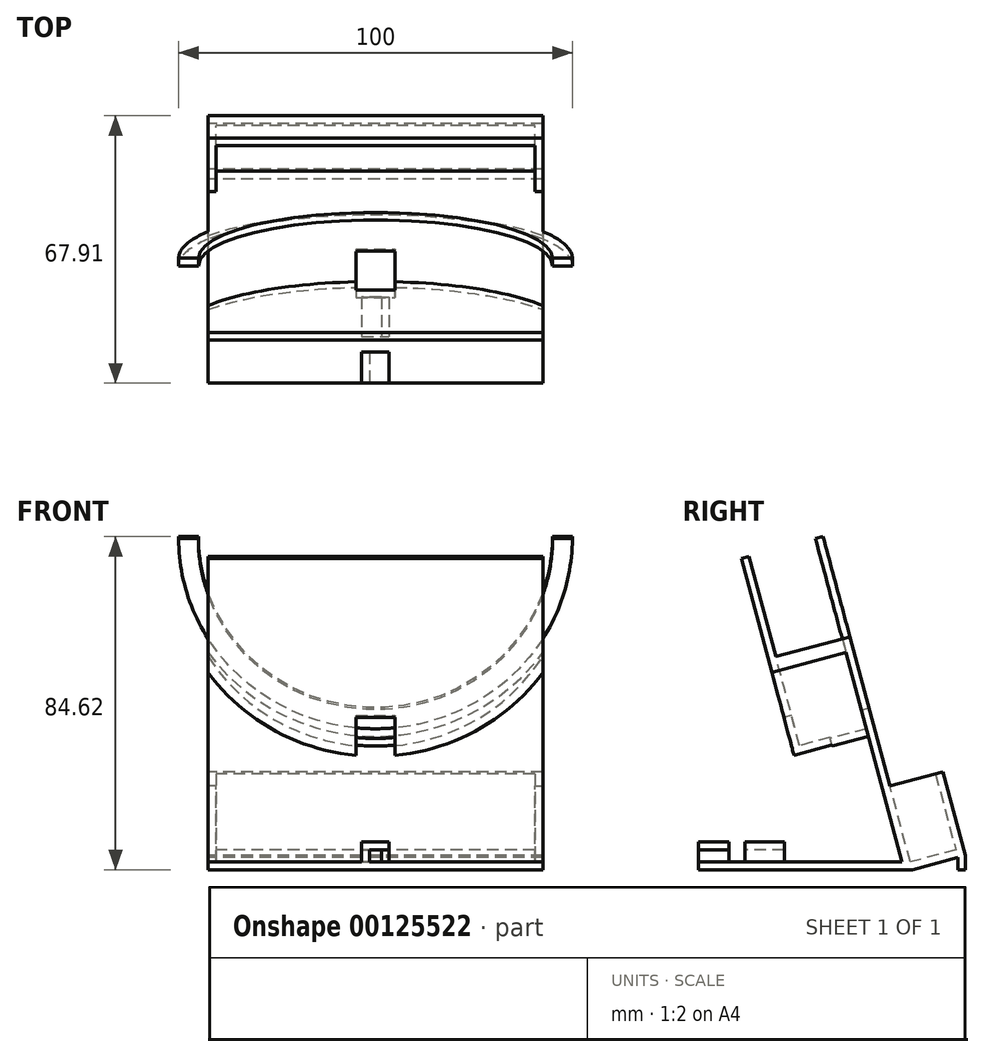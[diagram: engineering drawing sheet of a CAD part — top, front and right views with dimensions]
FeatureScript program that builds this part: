
annotation { "Feature Type Name" : "Feature", "Feature Type Description" : "" }
export const myFeature = defineFeature(function(context is Context, id is Id, definition is map)
    precondition{}
    {
        {
            var Q0;
            Q0=qCreatedBy(makeId("Right.planeOp"),FACE);
            var sketch = newSketch(context, id + "F0", { "sketchPlane" : qUnion([Q0])});
            skLineSegment(sketch, "E0", {"start": v(-54.39, 0) * mm, "end": v(0, 0) * mm});
            skLineSegment(sketch, "E1", {"start": v(-0.52, 1.93) * mm, "end": v(-23.24, 86.73) * mm});
            skLineSegment(sketch, "E2", {"start": v(-23.24, 86.73) * mm, "end": v(-25.17, 86.21) * mm});
            skLineSegment(sketch, "E3", {"start": v(-25.17, 86.21) * mm, "end": v(-2.6, 2) * mm});
            skLineSegment(sketch, "E4", {"start": v(-54.39, 0) * mm, "end": v(-54.39, 2) * mm});
            skLineSegment(sketch, "E5", {"start": v(-54.39, 2) * mm, "end": v(-2.6, 2) * mm});
            skLineSegment(sketch, "E6", {"start": v(0, 0) * mm, "end": v(11.52, 3.09) * mm});
            skLineSegment(sketch, "E7", {"start": v(13.52, 3.62) * mm, "end": v(13, 5.56) * mm});
            skLineSegment(sketch, "E8", {"start": v(11.07, 5.04) * mm, "end": v(-0.52, 1.93) * mm});
            skLineSegment(sketch, "E9", {"start": v(13, 5.56) * mm, "end": v(7.83, 24.87) * mm});
            skLineSegment(sketch, "E10", {"start": v(7.83, 24.87) * mm, "end": v(5.9, 24.36) * mm});
            skLineSegment(sketch, "E11", {"start": v(5.9, 24.36) * mm, "end": v(11.07, 5.04) * mm});
            skLineSegment(sketch, "E12", {"start": v(-65.45, 0) * mm, "end": v(42.7, 0) * mm, "construction": true});
            skLineSegment(sketch, "E13", {"start": v(13.52, 3.62) * mm, "end": v(13.52, 0) * mm});
            skLineSegment(sketch, "E14", {"start": v(13.52, 0) * mm, "end": v(11.52, 0) * mm});
            skLineSegment(sketch, "E15", {"start": v(11.52, 0) * mm, "end": v(11.52, 3.09) * mm});
            skSolve(sketch);
        }
        {
            var Q0;
            Q0 = qSketchRegion(id + "F0", true);
            extrude(context, id + "F1", {"entities" : qUnion([Q0]), "depth" : 85 * mm});
        }
        {
            var Q0;
            Q0=makeQuery(id+"F1.opExtrude","CAP_FACE",FACE,{"disambiguationData":[OSD([sQuery(id+"F0.wireOp",EDGE,"E0"),sQuery(id+"F0.wireOp",EDGE,"E1"),sQuery(id+"F0.wireOp",EDGE,"E2"),sQuery(id+"F0.wireOp",EDGE,"E3"),sQuery(id+"F0.wireOp",EDGE,"E4"),sQuery(id+"F0.wireOp",EDGE,"E5"),sQuery(id+"F0.wireOp",EDGE,"E6"),sQuery(id+"F0.wireOp",EDGE,"E7"),sQuery(id+"F0.wireOp",EDGE,"E8"),sQuery(id+"F0.wireOp",EDGE,"E9"),sQuery(id+"F0.wireOp",EDGE,"E10"),sQuery(id+"F0.wireOp",EDGE,"E11"),sQuery(id+"F0.wireOp",EDGE,"E13"),sQuery(id+"F0.wireOp",EDGE,"E14"),sQuery(id+"F0.wireOp",EDGE,"E15")])],"isStart":false});
            var sketch = newSketch(context, id + "F2", { "sketchPlane" : qUnion([Q0])});
            skLineSegment(sketch, "E16.0", {"start": v(5.9, 24.36) * mm, "end": v(11.07, 5.04) * mm});
            skLineSegment(sketch, "E16.1", {"start": v(11.07, 5.04) * mm, "end": v(-0.52, 1.93) * mm});
            skLineSegment(sketch, "E16.2", {"start": v(-0.52, 1.93) * mm, "end": v(-23.24, 86.73) * mm});
            skPoint(sketch, "E16.3", {"position": v(5.9, 24.36) * mm});
            skLineSegment(sketch, "E17", {"start": v(5.9, 24.36) * mm, "end": v(-5.7, 21.25) * mm});
            skSolve(sketch);
        }
        {
            var Q0;
            Q0 = qSketchRegion(id + "F2", true);
            extrude(context, id + "F3", {"entities" : qUnion([Q0]), "operationType" : NewBodyOperationType.ADD, "oppositeDirection" : true, "depth" : 2 * mm});
        }
        {
            var Q0;
            Q0=makeQuery(id+"F1.opExtrude","CAP_FACE",FACE,{"disambiguationData":[OSD([sQuery(id+"F0.wireOp",EDGE,"E0"),sQuery(id+"F0.wireOp",EDGE,"E1"),sQuery(id+"F0.wireOp",EDGE,"E2"),sQuery(id+"F0.wireOp",EDGE,"E3"),sQuery(id+"F0.wireOp",EDGE,"E4"),sQuery(id+"F0.wireOp",EDGE,"E5"),sQuery(id+"F0.wireOp",EDGE,"E6"),sQuery(id+"F0.wireOp",EDGE,"E7"),sQuery(id+"F0.wireOp",EDGE,"E8"),sQuery(id+"F0.wireOp",EDGE,"E9"),sQuery(id+"F0.wireOp",EDGE,"E10"),sQuery(id+"F0.wireOp",EDGE,"E11"),sQuery(id+"F0.wireOp",EDGE,"E13"),sQuery(id+"F0.wireOp",EDGE,"E14"),sQuery(id+"F0.wireOp",EDGE,"E15")])],"isStart":true});
            var sketch = newSketch(context, id + "F4", { "sketchPlane" : qUnion([Q0])});
            skLineSegment(sketch, "E18.0", {"start": v(-5.9, 24.36) * mm, "end": v(-11.07, 5.04) * mm});
            skLineSegment(sketch, "E18.1", {"start": v(-11.07, 5.04) * mm, "end": v(0.52, 1.93) * mm});
            skLineSegment(sketch, "E18.2", {"start": v(0.52, 1.93) * mm, "end": v(23.24, 86.73) * mm});
            skLineSegment(sketch, "E19", {"start": v(-5.9, 24.36) * mm, "end": v(5.7, 21.25) * mm});
            skSolve(sketch);
        }
        {
            var Q0;
            Q0 = qSketchRegion(id + "F4", true);
            extrude(context, id + "F5", {"entities" : qUnion([Q0]), "operationType" : NewBodyOperationType.ADD, "oppositeDirection" : true, "depth" : 2 * mm});
        }
        {
            var Q0;
            Q0=makeQuery(id+"F1.opExtrude","SWEPT_FACE",FACE,{"disambiguationData":[OSD([sQuery(id+"F0.wireOp",EDGE,"E3")])]});
            var sketch = newSketch(context, id + "F6", { "sketchPlane" : qUnion([Q0])});
            skLineSegment(sketch, "E20.0", {"start": v(85, 89.79) * mm, "end": v(0, 89.79) * mm});
            skLineSegment(sketch, "E21.0", {"start": v(0, 89.79) * mm, "end": v(0, 2.6) * mm});
            skLineSegment(sketch, "E22", {"start": v(0, 98.6) * mm, "end": v(85, 98.6) * mm, "construction": true});
            skLineSegment(sketch, "E23", {"start": v(96.81, 89.79) * mm, "end": v(96.81, 2.6) * mm, "construction": true});
            skPoint(sketch, "E24.endSnap0", {"position": v(42.5, 89.79) * mm});
            skCircle(sketch, "E25", {"center": v(42.5, 87.6) * mm, "radius": 50 * mm});
            skPoint(sketch, "E26", {"position": v(42.5, 37.6) * mm});
            skSolve(sketch);
        }
        {
            var Q0;
            Q0 = qSketchRegion(id + "F6", true);
            extrude(context, id + "F7", {"entities" : qUnion([Q0]), "operationType" : NewBodyOperationType.REMOVE, "oppositeDirection" : true, "depth" : 25 * mm});
        }
        {
            var Q0;
            Q0=makeQuery(id+"F1.opExtrude","SWEPT_FACE",FACE,{"disambiguationData":[OSD([sQuery(id+"F0.wireOp",EDGE,"E3")])]});
            var sketch = newSketch(context, id + "F8", { "sketchPlane" : qUnion([Q0])});
            skArc(sketch, "E27.0", {"start": v(0, 61.27) * mm, "mid": v(42.5, 37.6) * mm, "end": v(85, 61.27) * mm});
            skArc(sketch, "E28.0", {"start": v(0, 57.64) * mm, "mid": v(42.5, 35.6) * mm, "end": v(85, 57.64) * mm});
            skLineSegment(sketch, "E29.0", {"start": v(0, 61.27) * mm, "end": v(0, 2.6) * mm});
            skLineSegment(sketch, "E29.1", {"start": v(85, 61.27) * mm, "end": v(85, 2.6) * mm});
            skSolve(sketch);
        }
        {
            var Q0;
            Q0 = qSketchRegion(id + "F8", true);
            extrude(context, id + "F9", {"entities" : qUnion([Q0]), "operationType" : NewBodyOperationType.ADD, "depth" : 17.5 * mm});
        }
        {
            var Q0;
            Q0=makeQuery(id+"F9.opExtrude","CAP_FACE",FACE,{"disambiguationData":[OSD([sQuery(id+"F8.wireOp",EDGE,"E27.0"),sQuery(id+"F8.wireOp",EDGE,"E28.0"),sQuery(id+"F8.wireOp",EDGE,"E29.0"),sQuery(id+"F8.wireOp",EDGE,"E29.1")])],"isStart":false});
            var sketch = newSketch(context, id + "F10", { "sketchPlane" : qUnion([Q0])});
            skArc(sketch, "E30.0", {"start": v(0, 57.64) * mm, "mid": v(42.5, 35.6) * mm, "end": v(85, 57.64) * mm});
            skLineSegment(sketch, "E30.1", {"start": v(0, 61.27) * mm, "end": v(0, 57.64) * mm});
            skLineSegment(sketch, "E30.2", {"start": v(85, 61.27) * mm, "end": v(85, 57.64) * mm});
            skLineSegment(sketch, "E31", {"start": v(0, 61.27) * mm, "end": v(0, 87.6) * mm});
            skLineSegment(sketch, "E32", {"start": v(85, 61.27) * mm, "end": v(85, 87.6) * mm});
            skLineSegment(sketch, "E33", {"start": v(85, 87.6) * mm, "end": v(0, 87.6) * mm});
            skSolve(sketch);
        }
        {
            var Q0;
            Q0 = qSketchRegion(id + "F10", true);
            extrude(context, id + "F11", {"entities" : qUnion([Q0]), "operationType" : NewBodyOperationType.ADD, "depth" : 2 * mm});
        }
        {
            var Q0;
            Q0=makeQuery(id+"F11.opExtrude","CAP_FACE",FACE,{"disambiguationData":[OSD([sQuery(id+"F10.wireOp",EDGE,"E30.0"),sQuery(id+"F10.wireOp",EDGE,"E30.1"),sQuery(id+"F10.wireOp",EDGE,"E30.2"),sQuery(id+"F10.wireOp",EDGE,"E31"),sQuery(id+"F10.wireOp",EDGE,"E32"),sQuery(id+"F10.wireOp",EDGE,"E33")])],"isStart":false});
            var sketch = newSketch(context, id + "F12", { "sketchPlane" : qUnion([Q0])});
            skArc(sketch, "E34.0", {"start": v(0, 57.64) * mm, "mid": v(42.5, 35.6) * mm, "end": v(85, 57.64) * mm});
            skLineSegment(sketch, "E35", {"start": v(0, 57.64) * mm, "end": v(85, 57.64) * mm, "construction": true});
            skPoint(sketch, "E36", {"position": v(42.5, 57.64) * mm});
            skLineSegment(sketch, "E37", {"start": v(42.5, 57.64) * mm, "end": v(42.5, 35.6) * mm, "construction": true});
            skLineSegment(sketch, "E38", {"start": v(47.5, 57.64) * mm, "end": v(47.5, 35.85) * mm, "construction": true});
            skLineSegment(sketch, "E39", {"start": v(37.5, 57.64) * mm, "end": v(37.5, 35.85) * mm, "construction": true});
            skLineSegment(sketch, "E40", {"start": v(37.5, 35.85) * mm, "end": v(37.5, 45.85) * mm});
            skLineSegment(sketch, "E41", {"start": v(37.5, 45.85) * mm, "end": v(47.5, 45.85) * mm});
            skLineSegment(sketch, "E42", {"start": v(47.5, 45.85) * mm, "end": v(47.5, 35.85) * mm});
            skSolve(sketch);
        }
        {
            var Q0;
            Q0 = qSketchRegion(id + "F12", true);
            extrude(context, id + "F13", {"entities" : qUnion([Q0]), "operationType" : NewBodyOperationType.REMOVE, "oppositeDirection" : true, "depth" : 10 * mm});
        }
        {
            var Q0;
            Q0=makeQuery(id+"F1.opExtrude","SWEPT_FACE",FACE,{"disambiguationData":[OSD([sQuery(id+"F0.wireOp",EDGE,"E1")])]});
            var sketch = newSketch(context, id + "F14", { "sketchPlane" : qUnion([Q0])});
            skArc(sketch, "E43.0", {"start": v(7.5, 87.6) * mm, "mid": v(-42.5, 37.6) * mm, "end": v(-92.5, 87.6) * mm});
            skArc(sketch, "E44.0", {"start": v(2.5, 87.6) * mm, "mid": v(-42.5, 42.6) * mm, "end": v(-87.5, 87.6) * mm});
            skPoint(sketch, "E45.orphan", {"position": v(-85, 61.27) * mm});
            skPoint(sketch, "E46.orphan", {"position": v(0, 61.27) * mm});
            skLineSegment(sketch, "E47", {"start": v(-107.52, 87.6) * mm, "end": v(17.74, 87.6) * mm, "construction": true});
            skLineSegment(sketch, "E48", {"start": v(-92.5, 87.6) * mm, "end": v(-87.5, 87.6) * mm});
            skLineSegment(sketch, "E49", {"start": v(2.5, 87.6) * mm, "end": v(7.5, 87.6) * mm});
            skSolve(sketch);
        }
        {
            var Q0;
            Q0 = qSketchRegion(id + "F14", true);
            extrude(context, id + "F15", {"entities" : qUnion([Q0]), "operationType" : NewBodyOperationType.ADD, "oppositeDirection" : true, "depth" : 2 * mm});
        }
        {
            var Q0;
            Q0=makeQuery(id+"F1.opExtrude","SWEPT_FACE",FACE,{"disambiguationData":[OSD([sQuery(id+"F0.wireOp",EDGE,"E5")])]});
            var sketch = newSketch(context, id + "F16", { "sketchPlane" : qUnion([Q0])});
            skLineSegment(sketch, "E50.0", {"start": v(85, -2.6) * mm, "end": v(0, -2.6) * mm});
            skLineSegment(sketch, "E51.0", {"start": v(85, -54.39) * mm, "end": v(0, -54.39) * mm});
            skLineSegment(sketch, "E52", {"start": v(0, -54.39) * mm, "end": v(85, -54.39) * mm, "construction": true});
            skLineSegment(sketch, "E53", {"start": v(42.5, -54.39) * mm, "end": v(42.5, -2.6) * mm, "construction": true});
            skLineSegment(sketch, "E54.bottom", {"start": v(39, -32.54) * mm, "end": v(46, -32.54) * mm});
            skLineSegment(sketch, "E54.top", {"start": v(39, -42.54) * mm, "end": v(46, -42.54) * mm});
            skLineSegment(sketch, "E54.left", {"start": v(39, -32.54) * mm, "end": v(39, -42.54) * mm});
            skLineSegment(sketch, "E54.right", {"start": v(46, -32.54) * mm, "end": v(46, -42.54) * mm});
            skSolve(sketch);
        }
        {
            var Q0;
            Q0 = qSketchRegion(id + "F16", true);
            extrude(context, id + "F17", {"entities" : qUnion([Q0]), "operationType" : NewBodyOperationType.ADD, "depth" : 5 * mm});
        }
        {
            var Q0;
            Q0=makeQuery(id+"F17.opExtrude","SWEPT_FACE",FACE,{"disambiguationData":[OSD([sQuery(id+"F16.wireOp",EDGE,"E54.top")])]});
            var sketch = newSketch(context, id + "F18", { "sketchPlane" : qUnion([Q0])});
            skLineSegment(sketch, "E55", {"start": v(39, 5) * mm, "end": v(44, 5) * mm});
            skLineSegment(sketch, "E56", {"start": v(44, 5) * mm, "end": v(44, 2) * mm});
            skLineSegment(sketch, "E57.0", {"start": v(39, 7) * mm, "end": v(39, 2) * mm});
            skLineSegment(sketch, "E57.1", {"start": v(85, 2) * mm, "end": v(0, 2) * mm});
            skSolve(sketch);
        }
        {
            var Q0;
            Q0 = qSketchRegion(id + "F18", true);
            extrude(context, id + "F19", {"entities" : qUnion([Q0]), "operationType" : NewBodyOperationType.REMOVE, "oppositeDirection" : true, "depth" : 25 * mm});
        }
        {
            var Q0;
            Q0=makeQuery(id+"F19.boolean.opBoolean","MERGE",FACE,{"derivedFrom":[makeQuery(id+"F1.opExtrude","SWEPT_FACE",FACE,{"disambiguationData":[OSD([sQuery(id+"F0.wireOp",EDGE,"E5")])]}),makeQuery(id+"F19.opExtrude","SWEPT_FACE",FACE,{"disambiguationData":[OSD([sQuery(id+"F18.wireOp",EDGE,"E57.1")])]})]});
            var sketch = newSketch(context, id + "F20", { "sketchPlane" : qUnion([Q0])});
            skLineSegment(sketch, "E58.0", {"start": v(39, -32.54) * mm, "end": v(39, -42.54) * mm});
            skLineSegment(sketch, "E58.1", {"start": v(46, -32.54) * mm, "end": v(46, -42.54) * mm});
            skLineSegment(sketch, "E59.bottom", {"start": v(39, -54.39) * mm, "end": v(46, -54.39) * mm});
            skLineSegment(sketch, "E59.top", {"start": v(39, -46.54) * mm, "end": v(46, -46.54) * mm});
            skLineSegment(sketch, "E59.left", {"start": v(39, -54.39) * mm, "end": v(39, -46.54) * mm});
            skLineSegment(sketch, "E59.right", {"start": v(46, -54.39) * mm, "end": v(46, -46.54) * mm});
            skSolve(sketch);
        }
        {
            var Q0;
            Q0 = qSketchRegion(id + "F20", true);
            extrude(context, id + "F21", {"entities" : qUnion([Q0]), "operationType" : NewBodyOperationType.ADD, "depth" : 5 * mm});
        }
        {
            var Q0;
            Q0=makeQuery(id+"F21.boolean.opBoolean","MERGE",FACE,{"derivedFrom":[makeQuery(id+"F1.opExtrude","SWEPT_FACE",FACE,{"disambiguationData":[OSD([sQuery(id+"F0.wireOp",EDGE,"E4")])]}),makeQuery(id+"F21.opExtrude","SWEPT_FACE",FACE,{"disambiguationData":[OSD([sQuery(id+"F20.wireOp",EDGE,"E59.bottom")])]})]});
            var sketch = newSketch(context, id + "F22", { "sketchPlane" : qUnion([Q0])});
            skLineSegment(sketch, "E60.bottom", {"start": v(46, 2) * mm, "end": v(41, 2) * mm});
            skLineSegment(sketch, "E60.top", {"start": v(46, 5) * mm, "end": v(41, 5) * mm});
            skLineSegment(sketch, "E60.left", {"start": v(46, 2) * mm, "end": v(46, 5) * mm});
            skLineSegment(sketch, "E60.right", {"start": v(41, 2) * mm, "end": v(41, 5) * mm});
            skSolve(sketch);
        }
        {
            var Q0;
            Q0 = qSketchRegion(id + "F22", true);
            extrude(context, id + "F23", {"entities" : qUnion([Q0]), "operationType" : NewBodyOperationType.REMOVE, "oppositeDirection" : true, "depth" : 8 * mm});
        }
    });
